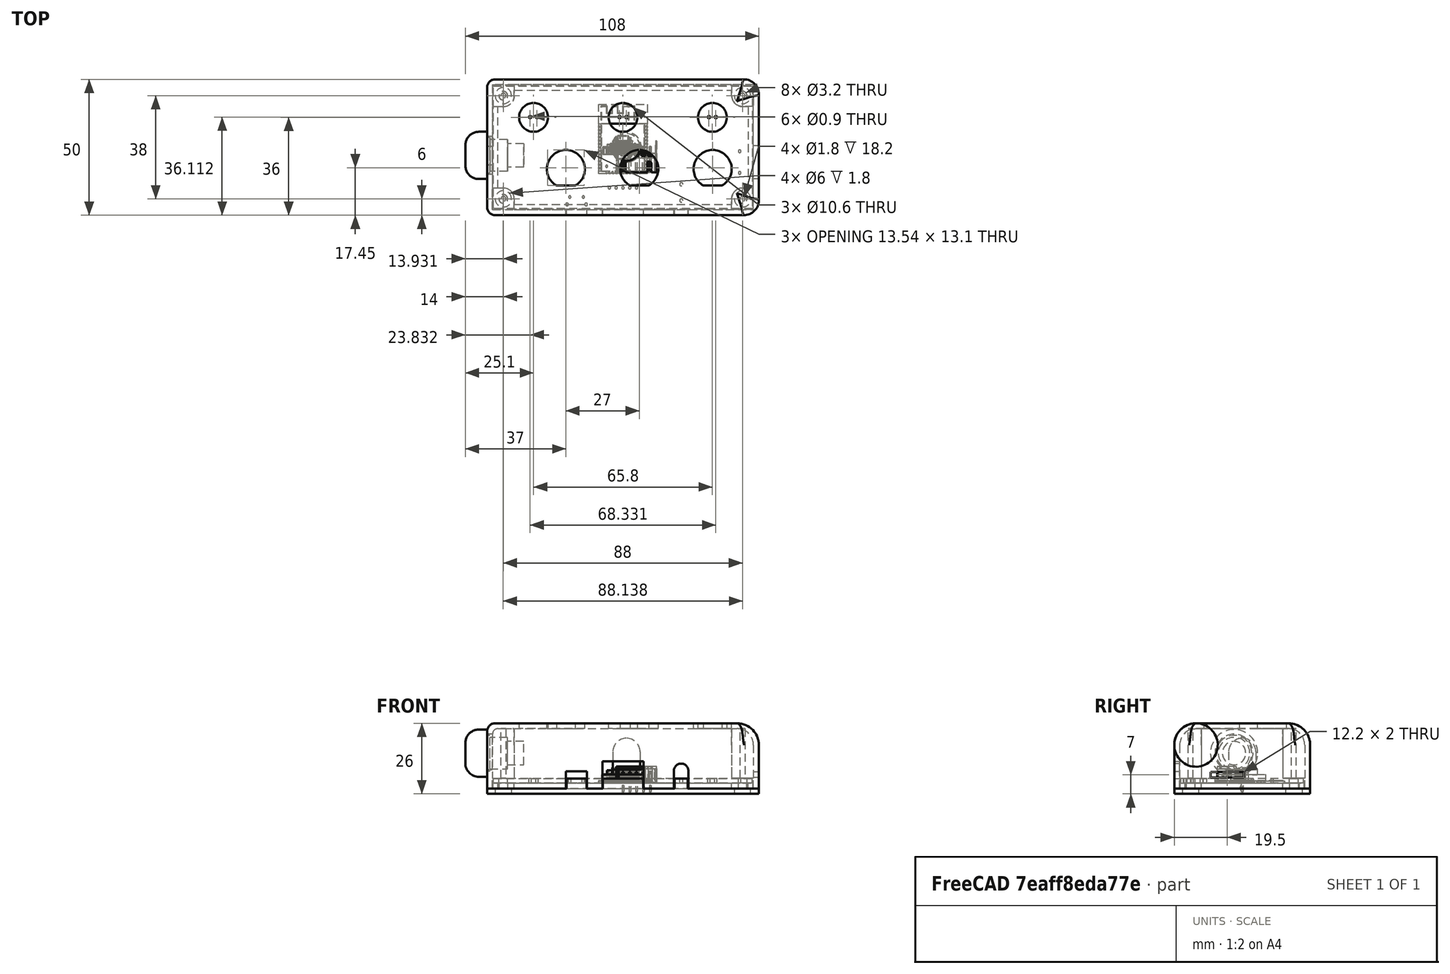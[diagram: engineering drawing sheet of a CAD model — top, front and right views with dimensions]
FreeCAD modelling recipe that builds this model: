
FCSTD DOCUMENT  (FreeCAD 0.21R33694 (Git))
Label: sigplane-head
License: All rights reserved
LicenseURL: http://en.wikipedia.org/wiki/All_rights_reserved
objects: Part::Feature×64, App::Part×58, Sketcher::SketchObject×16, PartDesign::Pad×9, PartDesign::Fillet×8, PartDesign::Pocket×7, PartDesign::Body×3, Part::FeaturePython×2, Mesh::Feature×1, App::DocumentObjectGroup×1
note: 132 computed .brp shape members not serialized (recipe doc carries the construction recipe); baked Part::Feature solids carry a one-line shape summary decoded from their .brp

FEATURE [Part::Feature] Part__Feature  label="SOLID"
  shape: bbox 2.5 x 3 x 1.2 mm, 76 faces (baked)
FEATURE [App::Part] SOT_23  label="SOT-23"
  Group = -> [Part__Feature]
  Origin = -> Origin
  Placement = pos=(20.265,16.3805,1.65) rot=(0,0,1;0rad)
FEATURE [Part::Feature] Part__Feature001  label="SOLID001"
  shape: bbox 2 x 1.2 x 0.45 mm, 26 faces (baked)
FEATURE [App::Part] R_0805_2012Metric
  Group = -> [Part__Feature001]
  Origin = -> Origin001
  Placement = pos=(-25.5505,-5.7785,1.65) rot=(0,0,1;0rad)
FEATURE [Part::Feature] Part__Feature002  label="SOLID002"
  shape: bbox 2 x 2 x 1.05 mm, 118 faces (baked)
FEATURE [App::Part] SOT_363_SC_70_6  label="SOT-363_SC-70-6"
  Group = -> [Part__Feature002]
  Origin = -> Origin002
  Placement = pos=(-20.762,-6.4135,1.65) rot=(0,0,1;0rad)
FEATURE [Part::Feature] Part__Feature003  label="SOLID003"
  shape: bbox 2 x 1.25 x 1.25 mm, 28 faces (baked)
FEATURE [App::Part] C_0805_2012Metric
  Group = -> [Part__Feature003]
  Origin = -> Origin003
  Placement = pos=(23.4885,10.2845,1.65) rot=(0,0,-1;1.5708rad)
FEATURE [Part::Feature] Part__Feature004  label="SOLID004"
  shape: bbox 15.15 x 4.2 x 4.7 mm, 267 faces (baked)
FEATURE [App::Part] Molex_PicoBlade_53398_0871_1x08_1MP_P1_25mm_Vertical  label="Molex_PicoBlade_53398-0871_1x08-1MP_P1.25mm_Vertical"
  Group = -> [Part__Feature004]
  Origin = -> Origin004
  Placement = pos=(-30.283,-18.7125,1.65) rot=(0,0,1;0rad)
FEATURE [Part::Feature] Part__Feature005  label="SOLID005"
  shape: bbox 3.2 x 1.6 x 0.55 mm, 26 faces (baked)
FEATURE [App::Part] R_1206_3216Metric
  Group = -> [Part__Feature005]
  Origin = -> Origin005
  Placement = pos=(4.699,19.4945,1.65) rot=(0,0,-1;1.5708rad)
FEATURE [Part::Feature] Part__Feature006  label="SOLID006"
  shape: bbox 2.5 x 1.25 x 1.1 mm, 67 faces (baked)
FEATURE [App::Part] D_SOD_323  label="D_SOD-323"
  Group = -> [Part__Feature006]
  Origin = -> Origin006
  Placement = pos=(4.953,-9.4275,1.65) rot=(0,0,-1;1.5708rad)
FEATURE [Part::Feature] Part__Feature007  label="SOLID007"
  shape: bbox 2 x 1.2 x 0.45 mm, 26 faces (baked)
FEATURE [App::Part] R_0805_2012Metric001
  Group = -> [Part__Feature007]
  Origin = -> Origin007
  Placement = pos=(-37.719,18.8595,1.65) rot=(0,0,-1;1.5708rad)
FEATURE [Part::Feature] Part__Feature008  label="SOLID008"
  shape: bbox 2 x 1.25 x 1.25 mm, 28 faces (baked)
FEATURE [App::Part] C_0805_2012Metric001
  Group = -> [Part__Feature008]
  Origin = -> Origin008
  Placement = pos=(-39.7455,2.6645,1.65) rot=(0,0,-1;1.5708rad)
FEATURE [Part::Feature] Part__Feature009  label="SOLID009"
  shape: bbox 2 x 1.25 x 1.25 mm, 28 faces (baked)
FEATURE [App::Part] C_0805_2012Metric002
  Group = -> [Part__Feature009]
  Origin = -> Origin009
  Placement = pos=(-32.004,-0.9525,1.65) rot=(0,0,-1;1.5708rad)
FEATURE [Part::Feature] Part__Feature010  label="SOLID010"
  shape: bbox 2 x 1.25 x 1.25 mm, 28 faces (baked)
FEATURE [App::Part] C_0805_2012Metric003
  Group = -> [Part__Feature010]
  Origin = -> Origin010
  Placement = pos=(23.4885,16.3805,1.65) rot=(0,0,-1;1.5708rad)
FEATURE [Part::Feature] Part__Feature011  label="SOLID011"
  shape: bbox 2.5 x 1.25 x 1.1 mm, 67 faces (baked)
FEATURE [App::Part] D_SOD_324  label="D_SOD-324"
  Group = -> [Part__Feature011]
  Origin = -> Origin011
  Placement = pos=(-25.5505,-14.2875,1.65) rot=(0,0,1;0rad)
FEATURE [Part::Feature] Part__Feature012  label="SOLID012"
  shape: bbox 2 x 1.25 x 1.25 mm, 28 faces (baked)
FEATURE [App::Part] C_0805_2012Metric004
  Group = -> [Part__Feature012]
  Origin = -> Origin012
  Placement = pos=(-20.701,-10.7315,1.65) rot=(0,0,-1;1.5708rad)
FEATURE [Part::Feature] Part__Feature013  label="SOLID013"
  shape: bbox 2 x 1.2 x 0.45 mm, 26 faces (baked)
FEATURE [App::Part] R_0805_2012Metric002
  Group = -> [Part__Feature013]
  Origin = -> Origin013
  Placement = pos=(-35.658,-11.517,1.65) rot=(0,0,-1;1.5708rad)
FEATURE [Part::Feature] Part__Feature014  label="SOLID014"
  shape: bbox 2 x 1.2 x 0.45 mm, 26 faces (baked)
FEATURE [App::Part] R_0805_2012Metric003
  Group = -> [Part__Feature014]
  Origin = -> Origin014
  Placement = pos=(9.9295,15.0445,1.65) rot=(0,0,1;0rad)
FEATURE [Part::Feature] Part__Feature015  label="SOLID015"
  shape: bbox 2 x 1.2 x 0.45 mm, 26 faces (baked)
FEATURE [App::Part] R_0805_2012Metric004
  Group = -> [Part__Feature015]
  Origin = -> Origin015
  Placement = pos=(-32.708,-11.517,1.65) rot=(0,0,-1;1.5708rad)
FEATURE [Part::Feature] Part__Feature016  label="SOLID016"
  shape: bbox 2 x 1.25 x 1.25 mm, 28 faces (baked)
FEATURE [App::Part] C_0805_2012Metric005
  Group = -> [Part__Feature016]
  Origin = -> Origin016
  Placement = pos=(19.939,-4.2545,1.65) rot=(0,0,1;3.14159rad)
FEATURE [Part::Feature] Part__Feature017  label="SOLID017"
  shape: bbox 6 x 8.7 x 1.65 mm, 396 faces (baked)
FEATURE [App::Part] SSOP_24_3_9x8_7mm_P0_635mm  label="SSOP-24_3.9x8.7mm_P0.635mm"
  Group = -> [Part__Feature017]
  Origin = -> Origin017
  Placement = pos=(16.0655,2.0285,1.65) rot=(0,0,-1;1.5708rad)
FEATURE [Part::Feature] Part__Feature018  label="SOLID018"
  shape: bbox 2 x 1.25 x 1.25 mm, 28 faces (baked)
FEATURE [App::Part] C_0805_2012Metric006
  Group = -> [Part__Feature018]
  Origin = -> Origin018
  Placement = pos=(-42.545,2.6645,1.65) rot=(0,0,-1;1.5708rad)
FEATURE [Part::Feature] Part__Feature019  label="SOLID019"
  shape: bbox 2 x 1.2 x 0.45 mm, 26 faces (baked)
FEATURE [App::Part] R_0805_2012Metric005
  Group = -> [Part__Feature019]
  Origin = -> Origin019
  Placement = pos=(30.353,18.836,1.65) rot=(0,0,-1;1.5708rad)
FEATURE [Part::Feature] Part__Feature020  label="SOLID020"
  shape: bbox 2 x 1.2 x 0.45 mm, 26 faces (baked)
FEATURE [App::Part] R_0805_2012Metric006
  Group = -> [Part__Feature020]
  Origin = -> Origin020
  Placement = pos=(9.923,11.0465,1.65) rot=(0,0,1;0rad)
FEATURE [Part::Feature] Part__Feature021  label="SOLID021"
  shape: bbox 3.2 x 1.6 x 0.55 mm, 26 faces (baked)
FEATURE [App::Part] R_1206_3216Metric001
  Group = -> [Part__Feature021]
  Origin = -> Origin021
  Placement = pos=(37.592,19.4945,1.65) rot=(0,0,-1;1.5708rad)
FEATURE [Part::Feature] Part__Feature022  label="SOLID022"
  shape: bbox 2 x 1.2 x 0.45 mm, 26 faces (baked)
FEATURE [App::Part] R_0805_2012Metric007
  Group = -> [Part__Feature022]
  Origin = -> Origin022
  Placement = pos=(6.477,1.2065,1.65) rot=(0,0,1;0rad)
FEATURE [Part::Feature] Part__Feature023  label="SOLID023"
  shape: bbox 2 x 1.2 x 0.45 mm, 26 faces (baked)
FEATURE [App::Part] R_0805_2012Metric008
  Group = -> [Part__Feature023]
  Origin = -> Origin023
  Placement = pos=(28.067,18.836,1.65) rot=(0,0,-1;1.5708rad)
FEATURE [Part::Feature] Part__Feature024  label="SOLID024"
  shape: bbox 2 x 1.2 x 0.45 mm, 26 faces (baked)
FEATURE [App::Part] R_0805_2012Metric009
  Group = -> [Part__Feature024]
  Origin = -> Origin024
  Placement = pos=(-2.54,18.883,1.65) rot=(0,0,-1;1.5708rad)
FEATURE [Part::Feature] Part__Feature025  label="SOLID025"
  shape: bbox 2.5 x 3 x 1.2 mm, 76 faces (baked)
FEATURE [App::Part] SOT_024  label="SOT-024"
  Group = -> [Part__Feature025]
  Origin = -> Origin025
  Placement = pos=(20.265,10.2895,1.65) rot=(0,0,1;0rad)
FEATURE [Part::Feature] Part__Feature026  label="SOLID026"
  shape: bbox 10.5 x 11 x 18.5 mm, 16 faces (baked)
FEATURE [App::Part] LED_D10_0mm  label="LED_D10.0mm"
  Group = -> [Part__Feature026]
  Origin = -> Origin026
  Placement = pos=(-1.275,11.1125,1.65) rot=(0,0,1;0rad)
FEATURE [Part::Feature] Part__Feature027  label="SOLID027"
  shape: bbox 2 x 1.2 x 0.45 mm, 26 faces (baked)
FEATURE [App::Part] R_0805_2012Metric010
  Group = -> [Part__Feature027]
  Origin = -> Origin027
  Placement = pos=(-10.414,-14.264,1.65) rot=(0,0,-1;1.5708rad)
FEATURE [Part::Feature] Part__Feature028  label="SOLID028"
  shape: bbox 2 x 1.2 x 0.45 mm, 26 faces (baked)
FEATURE [App::Part] R_0805_2012Metric011
  Group = -> [Part__Feature028]
  Origin = -> Origin028
  Placement = pos=(-35.433,18.8595,1.65) rot=(0,0,-1;1.5708rad)
FEATURE [Part::Feature] Part__Feature029  label="SOLID029"
  shape: bbox 2 x 1.2 x 0.45 mm, 26 faces (baked)
FEATURE [App::Part] R_0805_2012Metric012
  Group = -> [Part__Feature029]
  Origin = -> Origin029
  Placement = pos=(-4.826,18.883,1.65) rot=(0,0,-1;1.5708rad)
FEATURE [Part::Feature] Part__Feature030  label="SOLID030"
  shape: bbox 10.5 x 11 x 18.5 mm, 16 faces (baked)
FEATURE [App::Part] LED_D10_0mm001  label="LED_D10.0mm001"
  Group = -> [Part__Feature030]
  Origin = -> Origin030
  Placement = pos=(-34.168,11.1125,1.65) rot=(0,0,1;0rad)
FEATURE [Part::Feature] Part__Feature031  label="SOLID031"
  shape: bbox 2 x 1.2 x 0.45 mm, 26 faces (baked)
FEATURE [App::Part] R_0805_2012Metric013
  Group = -> [Part__Feature031]
  Origin = -> Origin031
  Placement = pos=(-13.208,-14.264,1.65) rot=(0,0,-1;1.5708rad)
FEATURE [Part::Feature] Part__Feature032  label="SOLID032"
  shape: bbox 2 x 1.2 x 0.45 mm, 26 faces (baked)
FEATURE [App::Part] R_0805_2012Metric014
  Group = -> [Part__Feature032]
  Origin = -> Origin032
  Placement = pos=(-29.758,-11.517,1.65) rot=(0,0,-1;1.5708rad)
FEATURE [Part::Feature] Part__Feature033  label="SOLID033"
  shape: bbox 2.5 x 3 x 1.2 mm, 76 faces (baked)
FEATURE [App::Part] SOT_025  label="SOT-025"
  Group = -> [Part__Feature033]
  Origin = -> Origin033
  Placement = pos=(13.818,16.4415,1.65) rot=(0,0,1;0rad)
FEATURE [Part::Feature] Part__Feature034  label="SOLID034"
  shape: bbox 5 x 5 x 0.92 mm, 182 faces (baked)
FEATURE [App::Part] QFN_28_1EP_5x5mm_P0_5mm_EP3_35x3_35mm  label="QFN-28-1EP_5x5mm_P0.5mm_EP3.35x3.35mm"
  Group = -> [Part__Feature034]
  Origin = -> Origin034
  Placement = pos=(-13.499,-8.8505,1.65) rot=(0,0,1;0rad)
FEATURE [Part::Feature] Part__Feature035  label="SOLID035"
  shape: bbox 2 x 1.2 x 0.45 mm, 26 faces (baked)
FEATURE [App::Part] R_0805_2012Metric015
  Group = -> [Part__Feature035]
  Origin = -> Origin035
  Placement = pos=(-38.608,-11.517,1.65) rot=(0,0,-1;1.5708rad)
FEATURE [Part::Feature] Part__Feature036  label="SOLID036"
  shape: bbox 3.2 x 1.6 x 0.55 mm, 26 faces (baked)
FEATURE [App::Part] R_1206_3216Metric002
  Group = -> [Part__Feature036]
  Origin = -> Origin036
  Placement = pos=(-28.194,19.4945,1.65) rot=(0,0,-1;1.5708rad)
FEATURE [Part::Feature] Part__Feature037  label="SOLID037"
  shape: bbox 2 x 1.2 x 0.45 mm, 26 faces (baked)
FEATURE [App::Part] R_0805_2012Metric016
  Group = -> [Part__Feature037]
  Origin = -> Origin037
  Placement = pos=(17.0115,10.261,1.65) rot=(0,0,-1;1.5708rad)
FEATURE [Part::Feature] Part__Feature038  label="SOLID038"
  shape: bbox 2 x 1.2 x 0.45 mm, 26 faces (baked)
FEATURE [App::Part] R_0805_2012Metric017
  Group = -> [Part__Feature038]
  Origin = -> Origin038
  Placement = pos=(-7.493,-7.9375,1.65) rot=(0,0,1;0rad)
FEATURE [Part::Feature] Part__Feature039  label="SOLID039"
  shape: bbox 14.9 x 11.5 x 9.5 mm, 193 faces (baked)
FEATURE [App::Part] JST_XH_S5B_XH_A_1x05_P2_50mm_Horizontal  label="JST_XH_S5B-XH-A_1x05_P2.50mm_Horizontal"
  Group = -> [Part__Feature039]
  Origin = -> Origin039
  Placement = pos=(-5,-14.9015,1.65) rot=(0,0,1;0rad)
FEATURE [Part::Feature] Part__Feature040  label="SOLID040"
  shape: bbox 2 x 1.2 x 0.45 mm, 26 faces (baked)
FEATURE [App::Part] R_0805_2012Metric018
  Group = -> [Part__Feature040]
  Origin = -> Origin040
  Placement = pos=(-32.004,2.7305,1.65) rot=(0,0,-1;1.5708rad)
FEATURE [Part::Feature] Part__Feature041  label="SOLID041"
  shape: bbox 2.5 x 3 x 1.2 mm, 76 faces (baked)
FEATURE [App::Part] SOT_026  label="SOT-026"
  Group = -> [Part__Feature041]
  Origin = -> Origin041
  Placement = pos=(-31.623,19.827,1.65) rot=(0,0,1;1.5708rad)
FEATURE [Part::Feature] Part__Feature042  label="SOLID042"
  shape: bbox 2.5 x 1.25 x 1.1 mm, 67 faces (baked)
FEATURE [App::Part] D_SOD_325  label="D_SOD-325"
  Group = -> [Part__Feature042]
  Origin = -> Origin042
  Placement = pos=(-25.5505,-9.8425,1.65) rot=(0,0,1;0rad)
FEATURE [Part::Feature] Part__Feature043  label="SOLID043"
  shape: bbox 2 x 1.2 x 0.45 mm, 26 faces (baked)
FEATURE [App::Part] R_0805_2012Metric019
  Group = -> [Part__Feature043]
  Origin = -> Origin043
  Placement = pos=(9.9295,17.2035,1.65) rot=(0,0,1;0rad)
FEATURE [Part::Feature] Part__Feature044  label="SOLID044"
  shape: bbox 2 x 1.25 x 1.25 mm, 28 faces (baked)
FEATURE [App::Part] C_0805_2012Metric007
  Group = -> [Part__Feature044]
  Origin = -> Origin044
  Placement = pos=(29.591,-6.6675,1.65) rot=(0,0,-1;1.5708rad)
FEATURE [Part::Feature] Part__Feature045  label="SOLID045"
  shape: bbox 2 x 1.2 x 0.45 mm, 26 faces (baked)
FEATURE [App::Part] R_0805_2012Metric020
  Group = -> [Part__Feature045]
  Origin = -> Origin045
  Placement = pos=(17.0415,16.4415,1.65) rot=(0,0,-1;1.5708rad)
FEATURE [Part::Feature] Part__Feature046  label="SOLID046"
  shape: bbox 2 x 1.25 x 1.25 mm, 28 faces (baked)
FEATURE [App::Part] C_0805_2012Metric008
  Group = -> [Part__Feature046]
  Origin = -> Origin046
  Placement = pos=(-20.701,-14.5415,1.65) rot=(0,0,-1;1.5708rad)
FEATURE [Part::Feature] Part__Feature047  label="SOLID047"
  shape: bbox 2.5 x 3 x 1.2 mm, 76 faces (baked)
FEATURE [App::Part] SOT_027  label="SOT-027"
  Group = -> [Part__Feature047]
  Origin = -> Origin047
  Placement = pos=(34.163,19.827,1.65) rot=(0,0,1;1.5708rad)
FEATURE [Part::Feature] Part__Feature048  label="SOLID048"
  shape: bbox 2 x 1.2 x 0.45 mm, 26 faces (baked)
FEATURE [App::Part] R_0805_2012Metric021
  Group = -> [Part__Feature048]
  Origin = -> Origin048
  Placement = pos=(6.477,3.2385,1.65) rot=(0,0,1;0rad)
FEATURE [Part::Feature] Part__Feature049  label="SOLID049"
  shape: bbox 2 x 1.2 x 0.45 mm, 26 faces (baked)
FEATURE [App::Part] R_0805_2012Metric022
  Group = -> [Part__Feature049]
  Origin = -> Origin049
  Placement = pos=(-7.493,-5.7785,1.65) rot=(0,0,1;0rad)
FEATURE [Part::Feature] Part__Feature050  label="SOLID050"
  shape: bbox 7.5 x 4.6 x 2 mm, 40 faces (baked)
FEATURE [App::Part] CP_EIA_7343_20_Kemet_V  label="CP_EIA-7343-20_Kemet-V"
  Group = -> [Part__Feature050]
  Origin = -> Origin050
  Placement = pos=(-35.687,0.5715,1.65) rot=(0,0,-1;1.5708rad)
FEATURE [Part::Feature] Part__Feature051  label="SOLID051"
  shape: bbox 18 x 25.5 x 3.1 mm, 751 faces (baked)
FEATURE [App::Part] ESP32_WROOM_32  label="ESP32-WROOM-32"
  Group = -> [Part__Feature051]
  Origin = -> Origin051
  Placement = pos=(-16.337,6.5455,1.65) rot=(0,0,1;0rad)
FEATURE [Part::Feature] Part__Feature052  label="SOLID052"
  shape: bbox 10.5 x 11 x 18.5 mm, 16 faces (baked)
FEATURE [App::Part] LED_D10_0mm002  label="LED_D10.0mm002"
  Group = -> [Part__Feature052]
  Origin = -> Origin052
  Placement = pos=(31.623,11.1125,1.65) rot=(0,0,1;0rad)
FEATURE [Part::Feature] Part__Feature053  label="SOLID053"
  shape: bbox 2.8 x 2.9 x 1.55 mm, 109 faces (baked)
FEATURE [App::Part] SOT_23_5  label="SOT-23-5"
  Group = -> [Part__Feature053]
  Origin = -> Origin053
  Placement = pos=(-40.767,6.9215,1.65) rot=(0,0,-1;1.5708rad)
FEATURE [Part::Feature] Part__Feature054  label="SOLID054"
  shape: bbox 2.5 x 3 x 1.2 mm, 76 faces (baked)
FEATURE [App::Part] SOT_028  label="SOT-028"
  Group = -> [Part__Feature054]
  Origin = -> Origin054
  Placement = pos=(1.27,19.827,1.65) rot=(0,0,1;1.5708rad)
FEATURE [Part::Feature] Part__Feature055  label="SOLID055"
  shape: bbox 2.5 x 3 x 1.2 mm, 76 faces (baked)
FEATURE [App::Part] SOT_029  label="SOT-029"
  Group = -> [Part__Feature055]
  Origin = -> Origin055
  Placement = pos=(13.758,10.2185,1.65) rot=(0,0,1;0rad)
FEATURE [Part::Feature] Part__Feature056  label="sigplane-head PCB"
  shape: bbox 95.25 x 45.09 x 1.6 mm, 67 faces (baked)
FEATURE [App::Part] sigplane_head_1  label="sigplane-head 1"
  Group = -> [SOT_23,R_0805_2012Metric,SOT_363_SC_70_6,C_0805_2012Metric,Molex_PicoBlade_53398_0871_1x08_1MP_P1_25mm_Vertical,R_1206_3216Metric,D_SOD_323,R_0805_2012Metric001,C_0805_2012Metric001,C_0805_2012Metric002,C_0805_2012Metric003,D_SOD_324,C_0805_2012Metric004,R_0805_2012Metric002,R_0805_2012Metric003,R_0805_2012Metric004,C_0805_2012Metric005,SSOP_24_3_9x8_7mm_P0_635mm,C_0805_2012Metric006,+38 more]
  Origin = -> Origin056
FEATURE [Mesh::Feature] microsd
  Placement = pos=(31.7,-12.5,1.1) rot=(0.57735,0.57735,0.57735;2.0944rad)
FEATURE [Part::Feature] Part__Feature057  label="Micro USB-B Female 5Pin SMD"
  shape: bbox 0.3 x 1.55 x 4.2 mm, 15 faces (baked)
FEATURE [Part::Feature] Part__Feature058  label="Micro USB-B Female 5Pin SMD001"
  shape: bbox 0.3 x 1.55 x 4.2 mm, 15 faces (baked)
FEATURE [Part::Feature] Part__Feature059  label="Micro USB-B Female 5Pin SMD002"
  shape: bbox 0.3 x 1.55 x 4.2 mm, 15 faces (baked)
FEATURE [Part::Feature] Part__Feature060  label="Micro USB-B Female 5Pin SMD003"
  shape: bbox 0.3 x 1.55 x 4.2 mm, 15 faces (baked)
FEATURE [Part::Feature] Part__Feature061  label="Micro USB-B Female 5Pin SMD004"
  shape: bbox 0.3 x 1.55 x 4.2 mm, 15 faces (baked)
FEATURE [Part::Feature] Part__Feature062  label="Micro USB-B Female 5Pin SMD005"
  shape: bbox 6.9 x 2.4 x 4.15 mm, 176 faces (baked)
FEATURE [Part::Feature] Part__Feature063  label="Micro USB-B Female 5Pin SMD006"
  shape: bbox 8.172 x 3.786 x 5.619 mm, 257 faces (baked)
FEATURE [App::Part] Micro_USB_B_Female_5Pin_SMD  label="Micro USB-B Female 5Pin SMD007"
  Group = -> [Part__Feature057,Part__Feature058,Part__Feature059,Part__Feature060,Part__Feature061,Part__Feature062,Part__Feature063]
  Origin = -> Origin057
  Placement = pos=(-17.1,-18.1,2.85) rot=(1,0,0;1.5708rad)
FEATURE [Sketcher::SketchObject] Sketch  label="основные габариты"
  AttachmentOffset = pos=(0,0,-2) rot=(0,0,1;0rad)
  FullyConstrained = true
  MapMode = 5
  Placement = pos=(0,0,-2) rot=(0,0,1;0rad)
  Support = -> [XY_Plane058]
  sketch-geometry (4):
    g0: LineSegment StartX=-50 StartY=25 StartZ=0 EndX=50 EndY=25 EndZ=0
    g1: LineSegment StartX=50 StartY=25 StartZ=0 EndX=50 EndY=-25 EndZ=0
    g2: LineSegment StartX=50 StartY=-25 StartZ=0 EndX=-50 EndY=-25 EndZ=0
    g3: LineSegment StartX=-50 StartY=-25 StartZ=0 EndX=-50 EndY=25 EndZ=0
  constraints (11):
    c: Coincident(g0,g1)
    c: Coincident(g1,g2)
    c: Coincident(g2,g3)
    c: Coincident(g3,g0)
    c: Horizontal(g0)
    c: Horizontal(g2)
    c: Vertical(g1)
    c: Vertical(g3)
    c: Symmetric(g0,g1,g-1)
    c: Distance(g0) = 100
    c: Distance(g3) = 50
FEATURE [PartDesign::Pad] Pad
  Direction = (0,0,1)
  Length = 24
  Length2 = 10
  Profile = -> Sketch
  ReferenceAxis = -> Sketch [N_Axis]
  Type = 0
FEATURE [Sketcher::SketchObject] Sketch001  label="внутр"
  FullyConstrained = true
  MapMode = 5
  Placement = pos=(0,0,-2) rot=(1,0,0;3.14159rad)
  Support = -> [Pad]
  sketch-geometry (4):
    g0: LineSegment StartX=-48 StartY=23 StartZ=0 EndX=48 EndY=23 EndZ=0
    g1: LineSegment StartX=48 StartY=23 StartZ=0 EndX=48 EndY=-23 EndZ=0
    g2: LineSegment StartX=48 StartY=-23 StartZ=0 EndX=-48 EndY=-23 EndZ=0
    g3: LineSegment StartX=-48 StartY=-23 StartZ=0 EndX=-48 EndY=23 EndZ=0
  constraints (11):
    c: Coincident(g0,g1)
    c: Coincident(g1,g2)
    c: Coincident(g2,g3)
    c: Coincident(g3,g0)
    c: Horizontal(g0)
    c: Horizontal(g2)
    c: Vertical(g1)
    c: Vertical(g3)
    c: Distance(g3) = 46
    c: Distance(g0) = 96
    c: Symmetric(g0,g1,g-1)
FEATURE [PartDesign::Pocket] Pocket
  BaseFeature = -> Pad
  Direction = (0,0,1)
  Length = 22
  Length2 = 5
  Profile = -> Sketch001
  ReferenceAxis = -> Sketch001 [N_Axis]
  Type = 0
FEATURE [Sketcher::SketchObject] Sketch002
  ExternalGeometry = -> [Pocket]
  FullyConstrained = true
  MapMode = 5
  Placement = pos=(0,0,20) rot=(1,0,0;3.14159rad)
  Support = -> [Pocket]
  sketch-geometry (24):
    g0: LineSegment StartX=-48 StartY=23 StartZ=0 EndX=-40 EndY=23 EndZ=0
    g1: LineSegment StartX=-48 StartY=23 StartZ=0 EndX=-48 EndY=15 EndZ=0
    g2: Circle CenterX=-44 CenterY=19 CenterZ=0 NormalX=0 NormalY=0 NormalZ=1 AngleXU=0 Radius=0.9
    g3: ArcOfCircle CenterX=-44 CenterY=19 CenterZ=0 NormalX=0 NormalY=0 NormalZ=1 AngleXU=0 Radius=4 StartAngle=4.71239 EndAngle=6.28319
    g4: LineSegment StartX=-48 StartY=15 StartZ=0 EndX=-44 EndY=15 EndZ=0
    g5: LineSegment StartX=-40 StartY=23 StartZ=0 EndX=-40 EndY=19 EndZ=0
    g6: ArcOfCircle CenterX=44 CenterY=19 CenterZ=0 NormalX=0 NormalY=0 NormalZ=1 AngleXU=0 Radius=4 StartAngle=3.14159 EndAngle=4.71239
    g7: LineSegment StartX=48 StartY=23 StartZ=0 EndX=40 EndY=23 EndZ=0
    g8: LineSegment StartX=40 StartY=23 StartZ=0 EndX=40 EndY=19 EndZ=0
    g9: LineSegment StartX=48 StartY=23 StartZ=0 EndX=48 EndY=15 EndZ=0
    g10: LineSegment StartX=48 StartY=15 StartZ=0 EndX=44 EndY=15 EndZ=0
    g11: Circle CenterX=44 CenterY=19 CenterZ=0 NormalX=0 NormalY=0 NormalZ=1 AngleXU=0 Radius=0.9
    g12: ArcOfCircle CenterX=-44 CenterY=-19 CenterZ=0 NormalX=0 NormalY=0 NormalZ=1 AngleXU=0 Radius=4 StartAngle=0 EndAngle=1.5708
    g13: LineSegment StartX=-48 StartY=-23 StartZ=0 EndX=-40 EndY=-23 EndZ=0
    g14: LineSegment StartX=-40 StartY=-23 StartZ=0 EndX=-40 EndY=-19 EndZ=0
    g15: LineSegment StartX=-48 StartY=-23 StartZ=0 EndX=-48 EndY=-15 EndZ=0
    g16: LineSegment StartX=-48 StartY=-15 StartZ=0 EndX=-44 EndY=-15 EndZ=0
    g17: Circle CenterX=-44 CenterY=-19 CenterZ=0 NormalX=0 NormalY=0 NormalZ=1 AngleXU=0 Radius=0.9
    g18: ArcOfCircle CenterX=44 CenterY=-19 CenterZ=0 NormalX=0 NormalY=0 NormalZ=1 AngleXU=0 Radius=4 StartAngle=1.5708 EndAngle=3.14159
    g19: LineSegment StartX=48 StartY=-23 StartZ=0 EndX=48 EndY=-15 EndZ=0
    g20: LineSegment StartX=48 StartY=-15 StartZ=0 EndX=44 EndY=-15 EndZ=0
    g21: LineSegment StartX=48 StartY=-23 StartZ=0 EndX=40 EndY=-23 EndZ=0
    g22: LineSegment StartX=40 StartY=-23 StartZ=0 EndX=40 EndY=-19 EndZ=0
    g23: Circle CenterX=44 CenterY=-19 CenterZ=0 NormalX=0 NormalY=0 NormalZ=1 AngleXU=0 Radius=0.9
  constraints (70):
    c: Coincident(g0,g-3)
    c: Horizontal(g0)
    c: Coincident(g1,g0)
    c: Vertical(g1)
    c: Radius(g2) = 0.9
    c: DistanceX(g0,g2) = 4
    c: DistanceY(g2,g0) = 4
    c: Coincident(g3,g2)
    c: Coincident(g3,g0)
    c: Coincident(g3,g1)
    c: Radius(g3) = 4
    c: Coincident(g4,g1)
    c: Horizontal(g4)
    c: Coincident(g5,g0)
    c: Vertical(g5)
    c: Distance(g5) = 4
    c: Distance(g4) = 4
    c: Coincident(g3,g5)
    c: Coincident(g3,g4)
    c: Radius(g6) = 4
    c: DistanceX(g6,g-6) = 4
    c: DistanceY(g6,g-6) = 4
    c: Coincident(g7,g-6)
    c: Horizontal(g7)
    c: Coincident(g8,g7)
    c: Vertical(g8)
    c: Coincident(g9,g7)
    c: Vertical(g9)
    c: Coincident(g10,g9)
    c: Horizontal(g10)
    c: Distance(g8) = 4
    c: Distance(g10) = 4
    c: Coincident(g6,g8)
    c: Coincident(g6,g10)
    c: Coincident(g11,g6)
    c: Radius(g11) = 0.9
    c: Radius(g12) = 4
    c: DistanceY(g-4,g12) = 4
    c: DistanceX(g-4,g12) = 4
    c: Coincident(g13,g-4)
    c: Horizontal(g13)
    c: Coincident(g14,g13)
    c: Vertical(g14)
    c: Coincident(g15,g13)
    c: Vertical(g15)
    c: Coincident(g16,g15)
    c: Horizontal(g16)
    c: Distance(g16) = 4
    c: Distance(g14) = 4
    c: Coincident(g12,g16)
    c: Coincident(g12,g14)
    c: Coincident(g17,g12)
    c: Radius(g17) = 0.9
    c: Radius(g18) = 4
    c: DistanceY(g-5,g18) = 4
    c: DistanceX(g18,g-5) = 4
    c: Coincident(g19,g-5)
    c: Vertical(g19)
    c: Coincident(g20,g19)
    c: Horizontal(g20)
    c: Coincident(g21,g19)
    c: Horizontal(g21)
    c: Vertical(g22)
    c: Distance(g22) = 4
    c: Distance(g20) = 4
    c: Coincident(g20,g18)
    c: Coincident(g18,g22)
    c: Coincident(g23,g18)
    c: Radius(g23) = 0.9
    c: Coincident(g22,g21)
FEATURE [PartDesign::Pad] Pad001  label="стойки винтов"
  BaseFeature = -> Pocket
  Direction = (0,0,-1)
  Length = 18.2
  Length2 = 10
  Profile = -> Sketch002
  ReferenceAxis = -> Sketch002 [N_Axis]
  Type = 0
FEATURE [Sketcher::SketchObject] Sketch003  label="резьба"
  FullyConstrained = true
  MapMode = 5
  Support = -> [XY_Plane059]
  sketch-geometry (1):
    g0: Circle CenterX=0 CenterY=0 CenterZ=0 NormalX=0 NormalY=0 NormalZ=1 AngleXU=0 Radius=5.8
  constraints (2):
    c: Coincident(g0,g-1)
    c: Diameter(g0) = 11.6
FEATURE [PartDesign::Pad] Pad002  label="pad-резьба"
  Direction = (0,0,1)
  Length = 7.5
  Length2 = 10
  Profile = -> Sketch003
  ReferenceAxis = -> Sketch003 [N_Axis]
  Type = 0
FEATURE [Sketcher::SketchObject] Sketch004  label="верхняя выпуклость"
  FullyConstrained = true
  MapMode = 5
  Support = -> [XY_Plane059]
  sketch-geometry (1):
    g0: Circle CenterX=0 CenterY=0 CenterZ=0 NormalX=0 NormalY=0 NormalZ=1 AngleXU=0 Radius=8.7
  constraints (2):
    c: Coincident(g0,g-1)
    c: Diameter(g0) = 17.4
FEATURE [PartDesign::Pad] Pad003  label="pad-верх"
  BaseFeature = -> Pad002
  Direction = (0,0,1)
  Length = 8
  Length2 = 10
  Profile = -> Sketch004
  ReferenceAxis = -> Sketch004 [N_Axis]
  Reversed = true
  Type = 0
  UseCustomVector = true
FEATURE [Sketcher::SketchObject] Sketch005  label="венец у резьбы"
  FullyConstrained = true
  MapMode = 5
  Support = -> [XY_Plane059]
  sketch-geometry (1):
    g0: Circle CenterX=0 CenterY=0 CenterZ=0 NormalX=0 NormalY=0 NormalZ=1 AngleXU=0 Radius=6.55
  constraints (2):
    c: Coincident(g0,g-1)
    c: Diameter(g0) = 13.1
FEATURE [PartDesign::Pad] Pad004  label="pad-венец"
  BaseFeature = -> Pad003
  Direction = (0,0,1)
  Length = 1
  Length2 = 10
  Profile = -> Sketch005
  ReferenceAxis = -> Sketch005 [N_Axis]
  Type = 0
FEATURE [Sketcher::SketchObject] Sketch007  label="контакты"
  FullyConstrained = true
  MapMode = 5
  Placement = pos=(0,0,7.5) rot=(0,0,1;0rad)
  Support = -> [Pad002]
  sketch-geometry (1):
    g0: Circle CenterX=0 CenterY=0 CenterZ=0 NormalX=0 NormalY=0 NormalZ=1 AngleXU=0 Radius=4.3
  constraints (2):
    c: Coincident(g0,g-1)
    c: Diameter(g0) = 8.6
FEATURE [PartDesign::Pad] Pad005  label="pad-контакты"
  BaseFeature = -> Pad004
  Direction = (0,0,1)
  Length = 6
  Length2 = 10
  Profile = -> Sketch007
  ReferenceAxis = -> Sketch007 [N_Axis]
  Type = 0
FEATURE [PartDesign::Fillet] Fillet002  label="Fill-верх"
  Base = -> Pad005 [Face3]
  BaseFeature = -> Pad005
  Radius = 5
  SupportTransform = false
  UseAllEdges = false
FEATURE [PartDesign::Body] Body001  label="кнопка"
  Group = -> [Sketch003,Sketch004,Pad002,Pad003,Sketch005,Pad004,Sketch007,Pad005,Fillet002]
  Origin = -> Origin059
  Placement = pos=(0,0,22) rot=(0,1,0;3.14159rad)
  Tip = -> Fillet002
FEATURE [Part::FeaturePython] Array  # Draft array (typed FeaturePython)
  AlwaysSyncPlacement = false
  Angle = 360
  ArrayType = 0
  Axis = (0,0,1)
  Base = -> Body001
  Center = (0,0,0)
  Count = 3
  ExpandArray = false
  Fuse = false
  IntervalAxis = (0,0,0)
  IntervalX = (27,0,0)
  IntervalY = (0,100,0)
  IntervalZ = (0,0,100)
  NumberCircles = 3
  NumberPolar = 5
  NumberX = 3
  NumberY = 1
  NumberZ = 1
  Placement = pos=(-21,-8,0) rot=(0,0,1;0rad)
  PlacementList = 3 placements: arithmetic series from (0,0,22) step (27,0,0) to (54,0,22)
  RadialDistance = 50
  ScaleList = (3) [(1,1,1),(1,1,1),(1,1,1)]
  Symmetry = 1
  TangentialDistance = 25
FEATURE [Part::FeaturePython] Clone  label="кнопка001"  # Draft clone (typed FeaturePython)
  AttacherType = Attacher::AttachEngine3D
  Fuse = false
  Objects = -> [Body001]
  Placement = pos=(-50,-3,11) rot=(0,1,0;1.5708rad)
  Scale = (1,1,1)
FEATURE [App::DocumentObjectGroup] Group  label="содержимое"
  Group = -> [sigplane_head_1,Micro_USB_B_Female_5Pin_SMD,microsd,Body001,Array,Clone]
FEATURE [Sketcher::SketchObject] Sketch008
  ExternalGeometry = -> [Pad001]
  FullyConstrained = true
  MapMode = 5
  Placement = pos=(0,0,22) rot=(0,0,1;0rad)
  Support = -> [Pad001]
  sketch-geometry (9):
    g0: Circle CenterX=-32.9 CenterY=11 CenterZ=0 NormalX=0 NormalY=0 NormalZ=1 AngleXU=0 Radius=5.3
    g1: Circle CenterX=4e-16 CenterY=11 CenterZ=0 NormalX=0 NormalY=0 NormalZ=1 AngleXU=0 Radius=5.3
    g2: Circle CenterX=32.9 CenterY=11 CenterZ=0 NormalX=0 NormalY=0 NormalZ=1 AngleXU=0 Radius=5.3
    g3: ArcOfCircle CenterX=-21 CenterY=-8 CenterZ=0 NormalX=0 NormalY=0 NormalZ=1 AngleXU=0 Radius=7 StartAngle=5.22508 EndAngle=10.4829
    g4: ArcOfCircle CenterX=6 CenterY=-8 CenterZ=0 NormalX=0 NormalY=0 NormalZ=1 AngleXU=0 Radius=7 StartAngle=5.22508 EndAngle=10.4829
    g5: ArcOfCircle CenterX=33 CenterY=-8 CenterZ=0 NormalX=0 NormalY=0 NormalZ=1 AngleXU=0 Radius=7 StartAngle=5.22508 EndAngle=10.4829
    g6: LineSegment StartX=-24.4337 StartY=-14.1 StartZ=0 EndX=-17.5663 EndY=-14.1 EndZ=0
    g7: LineSegment StartX=2.56634 StartY=-14.1 StartZ=0 EndX=9.43366 EndY=-14.1 EndZ=0
    g8: LineSegment StartX=29.5663 StartY=-14.1 StartZ=0 EndX=36.4337 EndY=-14.1 EndZ=0
  constraints (30):
    c: PointOnObject(g1,g-2)
    c: Radius(g0) = 5.3
    c: Radius(g1) = 5.3
    c: Radius(g2) = 5.3
    c: DistanceY(g0,g-3) = 14
    c: Horizontal(g0,g1)
    c: Horizontal(g1,g2)
    c: Distance(g1,g0) = 32.9
    c: Distance(g1,g2) = 32.9
    c: Horizontal(g3,g4)
    c: Horizontal(g4,g5)
    c: DistanceY(g3,g-1) = 8
    c: DistanceX(g3,g-1) = 21
    c: Distance(g3,g4) = 27
    c: Distance(g4,g5) = 27
    c: Radius(g3) = 7
    c: Radius(g4) = 7
    c: Radius(g5) = 7
    c: Coincident(g6,g3)
    c: Horizontal(g6)
    c: Coincident(g7,g4)
    c: Horizontal(g7)
    c: Coincident(g8,g5)
    c: Horizontal(g8)
    c: Coincident(g6,g3)
    c: Coincident(g7,g4)
    c: Coincident(g8,g5)
    c: DistanceY(g3,g3) = 6.1
    c: DistanceY(g4,g4) = 6.1
    c: DistanceY(g5,g5) = 6.1
FEATURE [PartDesign::Pocket] Pocket001  label="отверстия верх"
  BaseFeature = -> Pad001
  Direction = (0,0,-1)
  Length = 2
  Length2 = 5
  Profile = -> Sketch008
  ReferenceAxis = -> Sketch008 [N_Axis]
  Type = 0
FEATURE [Sketcher::SketchObject] Sketch009
  FullyConstrained = true
  MapMode = 5
  Placement = pos=(-50,0,0) rot=(0.57735,-0.57735,-0.57735;2.0944rad)
  Support = -> [Pocket001]
  sketch-geometry (2):
    g0: ArcOfCircle CenterX=3 CenterY=11 CenterZ=0 NormalX=0 NormalY=0 NormalZ=1 AngleXU=0 Radius=7 StartAngle=5.22508 EndAngle=10.4829
    g1: LineSegment StartX=-0.433657 StartY=4.9 StartZ=0 EndX=6.43366 EndY=4.9 EndZ=0
  constraints (7):
    c: Radius(g0) = 7
    c: DistanceY(g-1,g0) = 11
    c: DistanceX(g-1,g0) = 3
    c: Coincident(g1,g0)
    c: Horizontal(g1)
    c: Coincident(g1,g0)
    c: DistanceY(g0,g0) = 6.1
FEATURE [PartDesign::Pocket] Pocket002  label="отверстия бок кнопка"
  BaseFeature = -> Pocket001
  Direction = (1,0,0)
  Length = 2
  Length2 = 5
  Profile = -> Sketch009
  ReferenceAxis = -> Sketch009 [N_Axis]
  Type = 0
FEATURE [Sketcher::SketchObject] Sketch010
  ExternalGeometry = -> [Pocket002]
  FullyConstrained = true
  MapMode = 5
  Placement = pos=(50,0,0) rot=(0.57735,0.57735,0.57735;2.0944rad)
  Support = -> [Pocket002]
  sketch-geometry (4):
    g0: LineSegment StartX=-11.6 StartY=2 StartZ=0 EndX=0.6 EndY=2 EndZ=0
    g1: LineSegment StartX=0.6 StartY=2 StartZ=0 EndX=0.6 EndY=4 EndZ=0
    g2: LineSegment StartX=0.6 StartY=4 StartZ=0 EndX=-11.6 EndY=4 EndZ=0
    g3: LineSegment StartX=-11.6 StartY=4 StartZ=0 EndX=-11.6 EndY=2 EndZ=0
  constraints (12):
    c: Coincident(g0,g1)
    c: Coincident(g1,g2)
    c: Coincident(g2,g3)
    c: Coincident(g3,g0)
    c: Horizontal(g0)
    c: Horizontal(g2)
    c: Vertical(g1)
    c: Vertical(g3)
    c: Distance(g2) = 12.2
    c: DistanceX(g-1,g0) = 0.6
    c: DistanceY(g-1,g1) = 4
    c: DistanceY(g-1,g0) = 2
FEATURE [PartDesign::Pocket] Pocket003  label="отверстия sdcard"
  BaseFeature = -> Pocket002
  Direction = (-1,0,0)
  Length = 2
  Length2 = 5
  Profile = -> Sketch010
  ReferenceAxis = -> Sketch010 [N_Axis]
  Type = 0
FEATURE [Sketcher::SketchObject] Sketch011
  FullyConstrained = true
  MapMode = 5
  Placement = pos=(0,-25,0) rot=(1,0,0;1.5708rad)
  Support = -> [Pocket003]
  sketch-geometry (14):
    g0: LineSegment StartX=-21 StartY=-2 StartZ=0 EndX=-13.2 EndY=-2 EndZ=0
    g1: LineSegment StartX=-13.2 StartY=-2 StartZ=0 EndX=-13.2 EndY=4.3 EndZ=0
    g2: LineSegment StartX=-13.2 StartY=4.3 StartZ=0 EndX=-21 EndY=4.3 EndZ=0
    g3: LineSegment StartX=-21 StartY=4.3 StartZ=0 EndX=-21 EndY=-2 EndZ=0
    g4: LineSegment StartX=-7.6 StartY=-2 StartZ=0 EndX=7.6 EndY=-2 EndZ=0
    g5: LineSegment StartX=7.6 StartY=-2 StartZ=0 EndX=7.6 EndY=8 EndZ=0
    g6: LineSegment StartX=7.6 StartY=8 StartZ=0 EndX=-7.6 EndY=8 EndZ=0
    g7: LineSegment StartX=-7.6 StartY=8 StartZ=0 EndX=-7.6 EndY=-2 EndZ=0
    g8: LineSegment StartX=18.75 StartY=-2 StartZ=0 EndX=24.05 EndY=-2 EndZ=0
    g9: LineSegment StartX=24.05 StartY=-2 StartZ=0 EndX=24.05 EndY=4.5 EndZ=0
    g10: LineSegment StartX=18.75 StartY=4.5 StartZ=0 EndX=18.75 EndY=-2 EndZ=0
    g11: GeomPoint X=21.4 Y=-2 Z=0
    g12: ArcOfCircle CenterX=21.4 CenterY=4.5 CenterZ=0 NormalX=0 NormalY=0 NormalZ=1 AngleXU=0 Radius=2.65 StartAngle=1e-16 EndAngle=3.14159
    g13: GeomPoint X=-17.1 Y=-2 Z=0
  constraints (38):
    c: Coincident(g0,g1)
    c: Coincident(g1,g2)
    c: Coincident(g2,g3)
    c: Coincident(g3,g0)
    c: Horizontal(g0)
    c: Horizontal(g2)
    c: Vertical(g1)
    c: Vertical(g3)
    c: Coincident(g4,g5)
    c: Coincident(g5,g6)
    c: Coincident(g6,g7)
    c: Coincident(g7,g4)
    c: Horizontal(g4)
    c: Vertical(g5)
    c: Vertical(g7)
    c: Coincident(g8,g9)
    c: Coincident(g10,g8)
    c: Horizontal(g8)
    c: Vertical(g9)
    c: Vertical(g10)
    c: Distance(g4) = 15.2
    c: Distance(g8) = 5.3
    c: Symmetric(g8,g8,g11)
    c: Coincident(g12,g10)
    c: Coincident(g12,g9)
    c: Horizontal(g10,g12)
    c: Horizontal(g12,g9)
    c: DistanceY(g-1,g2) = 4.3
    c: DistanceY(g-1,g5) = 8
    c: DistanceY(g-1,g12) = 4.5
    c: Symmetric(g6,g5,g-2)
    c: DistanceX(g-1,g11) = 21.4
    c: Symmetric(g0,g0,g13)
    c: DistanceX(g13,g-1) = 17.1
    c: Horizontal(g0,g4)
    c: Horizontal(g4,g8)
    c: DistanceX(g0,g0) = 7.8
    c: DistanceY(g4,g-1) = 2
FEATURE [PartDesign::Pocket] Pocket004  label="отверстия низ"
  BaseFeature = -> Pocket003
  Direction = (0,1,-2e-16)
  Length = 2
  Length2 = 5
  Profile = -> Sketch011
  ReferenceAxis = -> Sketch011 [N_Axis]
  Type = 0
FEATURE [PartDesign::Fillet] Fillet  label="сглаж внутр"
  Base = -> Pocket004 [Edge83,Edge74,Edge87]
  BaseFeature = -> Pocket004
  Radius = 6
  SupportTransform = false
  UseAllEdges = false
FEATURE [PartDesign::Fillet] Fillet003  label="сглаж внутр лев"
  Base = -> Fillet [Edge61]
  BaseFeature = -> Fillet
  Radius = 2
  SupportTransform = false
  UseAllEdges = false
FEATURE [PartDesign::Fillet] Fillet004  label="сглаж верх"
  Base = -> Fillet003 [Edge109,Edge127,Edge108]
  BaseFeature = -> Fillet003
  Radius = 8
  SupportTransform = false
  UseAllEdges = false
FEATURE [PartDesign::Fillet] Fillet005  label="сглаж верх лев"
  Base = -> Fillet004 [Edge6,Edge8,Edge9]
  BaseFeature = -> Fillet004
  Radius = 3
  SupportTransform = false
  UseAllEdges = false
FEATURE [PartDesign::Fillet] Fillet006  label="сглаж бок"
  Base = -> Fillet005 [Edge13,Edge32,Edge6,Edge3]
  BaseFeature = -> Fillet005
  Radius = 5.5
  SupportTransform = false
  UseAllEdges = false
FEATURE [PartDesign::Body] Body  label="top"
  Group = -> [Sketch,Pad,Sketch001,Pocket,Sketch002,Pad001,Sketch008,Pocket001,Sketch009,Pocket002,Sketch010,Pocket003,Sketch011,Pocket004,Fillet,Fillet003,Fillet004,Fillet005,Fillet006]
  Origin = -> Origin058
  Tip = -> Fillet006
FEATURE [Sketcher::SketchObject] Sketch012
  AttachmentOffset = pos=(0,0,-2) rot=(0,0,1;0rad)
  FullyConstrained = true
  MapMode = 5
  Placement = pos=(0,0,-2) rot=(0,0,1;0rad)
  Support = -> [XY_Plane060]
  sketch-geometry (4):
    g0: LineSegment StartX=-50 StartY=25 StartZ=0 EndX=50 EndY=25 EndZ=0
    g1: LineSegment StartX=50 StartY=25 StartZ=0 EndX=50 EndY=-25 EndZ=0
    g2: LineSegment StartX=50 StartY=-25 StartZ=0 EndX=-50 EndY=-25 EndZ=0
    g3: LineSegment StartX=-50 StartY=-25 StartZ=0 EndX=-50 EndY=25 EndZ=0
  constraints (11):
    c: Coincident(g0,g1)
    c: Coincident(g1,g2)
    c: Coincident(g2,g3)
    c: Coincident(g3,g0)
    c: Horizontal(g0)
    c: Horizontal(g2)
    c: Vertical(g1)
    c: Vertical(g3)
    c: DistanceY(g3,g3) = 50
    c: DistanceX(g0,g0) = 100
    c: Symmetric(g0,g1,g-1)
FEATURE [PartDesign::Pad] Pad006  label="основа"
  Direction = (0,0,-1)
  Length = 2
  Length2 = 10
  Profile = -> Sketch012
  ReferenceAxis = -> Sketch012 [N_Axis]
  Type = 0
  UseCustomVector = true
FEATURE [Sketcher::SketchObject] Sketch013
  FullyConstrained = true
  MapMode = 5
  Placement = pos=(0,0,-2) rot=(0,0,1;0rad)
  Support = -> [Pad006]
  sketch-geometry (20):
    g0: LineSegment StartX=-47.8 StartY=22.8 StartZ=0 EndX=47.8 EndY=22.8 EndZ=0
    g1: LineSegment StartX=47.8 StartY=22.8 StartZ=0 EndX=47.8 EndY=-22.8 EndZ=0
    g2: LineSegment StartX=47.8 StartY=-22.8 StartZ=0 EndX=-47.8 EndY=-22.8 EndZ=0
    g3: LineSegment StartX=-47.8 StartY=-22.8 StartZ=0 EndX=-47.8 EndY=22.8 EndZ=0
    g4: ArcOfCircle CenterX=-44 CenterY=19 CenterZ=0 NormalX=0 NormalY=0 NormalZ=1 AngleXU=0 Radius=4 StartAngle=4.71239 EndAngle=6.28319
    g5: ArcOfCircle CenterX=44 CenterY=19 CenterZ=0 NormalX=0 NormalY=0 NormalZ=1 AngleXU=0 Radius=4 StartAngle=3.14159 EndAngle=4.71239
    g6: ArcOfCircle CenterX=-44 CenterY=-19 CenterZ=0 NormalX=0 NormalY=0 NormalZ=1 AngleXU=0 Radius=4 StartAngle=2.08076e-08 EndAngle=1.5708
    g7: ArcOfCircle CenterX=44 CenterY=-19 CenterZ=0 NormalX=0 NormalY=0 NormalZ=1 AngleXU=0 Radius=4 StartAngle=1.5708 EndAngle=3.14159
    g8: LineSegment StartX=-44 StartY=-15 StartZ=0 EndX=-46 EndY=-15 EndZ=0
    g9: LineSegment StartX=-40 StartY=-19 StartZ=0 EndX=-40 EndY=-21 EndZ=0
    g10: LineSegment StartX=-44 StartY=15 StartZ=0 EndX=-46 EndY=15 EndZ=0
    g11: LineSegment StartX=-40 StartY=19 StartZ=0 EndX=-40 EndY=21 EndZ=0
    g12: LineSegment StartX=40 StartY=19 StartZ=0 EndX=40 EndY=21 EndZ=0
    g13: LineSegment StartX=44 StartY=15 StartZ=0 EndX=46 EndY=15 EndZ=0
    g14: LineSegment StartX=44 StartY=-15 StartZ=0 EndX=46 EndY=-15 EndZ=0
    g15: LineSegment StartX=40 StartY=-19 StartZ=0 EndX=40 EndY=-21 EndZ=0
    g16: LineSegment StartX=-40 StartY=-21 StartZ=0 EndX=40 EndY=-21 EndZ=0
    g17: LineSegment StartX=-46 StartY=-15 StartZ=0 EndX=-46 EndY=15 EndZ=0
    g18: LineSegment StartX=-40 StartY=21 StartZ=0 EndX=40 EndY=21 EndZ=0
    g19: LineSegment StartX=46 StartY=15 StartZ=0 EndX=46 EndY=-15 EndZ=0
  constraints (63):
    c: Coincident(g0,g1)
    c: Coincident(g1,g2)
    c: Coincident(g2,g3)
    c: Coincident(g3,g0)
    c: Horizontal(g0)
    c: Horizontal(g2)
    c: Vertical(g1)
    c: Vertical(g3)
    c: DistanceX(g0,g0) = 95.6
    c: DistanceY(g3,g3) = 45.6
    c: Symmetric(g0,g1,g-1)
    c: DistanceY(g4,g0) = 3.8
    c: DistanceY(g2,g6) = 3.8
    c: DistanceX(g7,g1) = 3.8
    c: DistanceX(g0,g4) = 3.8
    c: Radius(g4) = 4
    c: Radius(g5) = 4
    c: Radius(g7) = 4
    c: Radius(g6) = 4
    c: Coincident(g8,g6)
    c: Horizontal(g8)
    c: Coincident(g9,g6)
    c: Vertical(g9)
    c: Coincident(g10,g4)
    c: Horizontal(g10)
    c: Coincident(g11,g4)
    c: Vertical(g11)
    c: Coincident(g12,g5)
    c: Vertical(g12)
    c: Coincident(g13,g5)
    c: Horizontal(g13)
    c: Coincident(g14,g7)
    c: Horizontal(g14)
    c: Coincident(g15,g7)
    c: Vertical(g15)
    c: DistanceX(g14,g14) = 2
    c: DistanceX(g8,g8) = 2
    c: DistanceX(g10,g10) = 2
    c: DistanceX(g13,g13) = 2
    c: DistanceY(g12,g12) = 2
    c: DistanceY(g11,g11) = 2
    c: DistanceY(g9,g9) = 2
    c: DistanceY(g15,g15) = 2
    c: Coincident(g16,g9)
    c: Horizontal(g16)
    c: Coincident(g17,g8)
    c: Vertical(g17)
    c: Coincident(g18,g11)
    c: Horizontal(g18)
    c: Coincident(g19,g13)
    c: Vertical(g19)
    c: Coincident(g17,g10)
    c: Coincident(g18,g12)
    c: Coincident(g19,g14)
    c: Coincident(g16,g15)
    c: DistanceX(g0,g10) = 1.8
    c: DistanceX(g14,g1) = 1.8
    c: DistanceX(g0,g11) = 7.8
    c: Vertical(g6,g4)
    c: Vertical(g6,g4)
    c: Horizontal(g6,g7)
    c: Vertical(g5,g7)
    c: Horizontal(g5,g4)
FEATURE [PartDesign::Pad] Pad007  label="внутр грань"
  BaseFeature = -> Pad006
  Direction = (0,0,1)
  Length = 2
  Length2 = 10
  Profile = -> Sketch013
  ReferenceAxis = -> Sketch013 [N_Axis]
  Type = 0
FEATURE [Sketcher::SketchObject] Sketch014
  FullyConstrained = true
  MapMode = 5
  Placement = pos=(0,0,-2) rot=(0,0,1;0rad)
  Support = -> [Pad007]
  sketch-geometry (14):
    g0: LineSegment StartX=-20.8 StartY=-22.8 StartZ=0 EndX=-13.4 EndY=-22.8 EndZ=0
    g1: LineSegment StartX=-13.4 StartY=-22.8 StartZ=0 EndX=-13.4 EndY=-25 EndZ=0
    g2: LineSegment StartX=-13.4 StartY=-25 StartZ=0 EndX=-20.8 EndY=-25 EndZ=0
    g3: LineSegment StartX=-20.8 StartY=-25 StartZ=0 EndX=-20.8 EndY=-22.8 EndZ=0
    g4: LineSegment StartX=-7.4 StartY=-22.8 StartZ=0 EndX=7.4 EndY=-22.8 EndZ=0
    g5: LineSegment StartX=7.4 StartY=-22.8 StartZ=0 EndX=7.4 EndY=-25 EndZ=0
    g6: LineSegment StartX=7.4 StartY=-25 StartZ=0 EndX=-7.4 EndY=-25 EndZ=0
    g7: LineSegment StartX=-7.4 StartY=-25 StartZ=0 EndX=-7.4 EndY=-22.8 EndZ=0
    g8: LineSegment StartX=18.95 StartY=-22.8 StartZ=0 EndX=23.85 EndY=-22.8 EndZ=0
    g9: LineSegment StartX=23.85 StartY=-22.8 StartZ=0 EndX=23.85 EndY=-25 EndZ=0
    g10: LineSegment StartX=23.85 StartY=-25 StartZ=0 EndX=18.95 EndY=-25 EndZ=0
    g11: LineSegment StartX=18.95 StartY=-25 StartZ=0 EndX=18.95 EndY=-22.8 EndZ=0
    g12: GeomPoint X=-17.1 Y=-25 Z=0
    g13: GeomPoint X=21.4 Y=-25 Z=0
  constraints (37):
    c: Coincident(g0,g1)
    c: Coincident(g1,g2)
    c: Coincident(g2,g3)
    c: Coincident(g3,g0)
    c: Horizontal(g0)
    c: Horizontal(g2)
    c: Vertical(g1)
    c: Vertical(g3)
    c: Coincident(g4,g5)
    c: Coincident(g5,g6)
    c: Coincident(g6,g7)
    c: Coincident(g7,g4)
    c: Horizontal(g4)
    c: Vertical(g5)
    c: Vertical(g7)
    c: Coincident(g8,g9)
    c: Coincident(g9,g10)
    c: Coincident(g10,g11)
    c: Coincident(g11,g8)
    c: Horizontal(g8)
    c: Horizontal(g10)
    c: Vertical(g9)
    c: Vertical(g11)
    c: DistanceY(g3,g3) = 2.2
    c: Horizontal(g1,g6)
    c: Horizontal(g5,g10)
    c: Horizontal(g0,g4)
    c: Horizontal(g4,g8)
    c: DistanceX(g6,g6) = 14.8
    c: DistanceX(g10,g10) = 4.9
    c: DistanceX(g2,g2) = 7.4
    c: Symmetric(g6,g5,g-2)
    c: DistanceX(g12,g-1) = 17.1
    c: DistanceX(g-1,g13) = 21.4
    c: Symmetric(g2,g1,g12)
    c: Symmetric(g10,g9,g13)
    c: DistanceY(g6,g-1) = 25
FEATURE [PartDesign::Pad] Pad008  label="заглушки нижних отверстий"
  BaseFeature = -> Pad007
  Direction = (0,0,1)
  Length = 3.6
  Length2 = 10
  Profile = -> Sketch014
  ReferenceAxis = -> Sketch014 [N_Axis]
  Type = 0
FEATURE [Sketcher::SketchObject] Sketch015
  ExternalGeometry = -> [Pad008]
  FullyConstrained = true
  MapMode = 5
  Placement = pos=(0,0,-4) rot=(1,0,0;3.14159rad)
  Support = -> [Pad008]
  sketch-geometry (4):
    g0: Circle CenterX=-44 CenterY=19 CenterZ=0 NormalX=0 NormalY=0 NormalZ=1 AngleXU=0 Radius=1.6
    g1: Circle CenterX=44 CenterY=19 CenterZ=0 NormalX=0 NormalY=0 NormalZ=1 AngleXU=0 Radius=1.6
    g2: Circle CenterX=-44 CenterY=-19 CenterZ=0 NormalX=0 NormalY=0 NormalZ=1 AngleXU=0 Radius=1.6
    g3: Circle CenterX=44 CenterY=-19 CenterZ=0 NormalX=0 NormalY=0 NormalZ=1 AngleXU=0 Radius=1.6
  constraints (12):
    c: Radius(g0) = 1.6
    c: Radius(g2) = 1.6
    c: Radius(g3) = 1.6
    c: Radius(g1) = 1.6
    c: DistanceX(g-3,g0) = 6
    c: DistanceX(g-4,g2) = 6
    c: DistanceX(g3,g-5) = 6
    c: DistanceX(g1,g-6) = 6
    c: DistanceY(g0,g-3) = 6
    c: DistanceY(g-4,g2) = 6
    c: DistanceY(g-5,g3) = 6
    c: DistanceY(g1,g-6) = 6
FEATURE [PartDesign::Pocket] Pocket005  label="отверстия"
  BaseFeature = -> Pad008
  Direction = (0,0,1)
  Length = 5
  Length2 = 5
  Profile = -> Sketch015
  ReferenceAxis = -> Sketch015 [N_Axis]
  Type = 1
FEATURE [Sketcher::SketchObject] Sketch016
  ExternalGeometry = -> [Pocket005]
  FullyConstrained = true
  MapMode = 5
  Placement = pos=(0,0,-4) rot=(1,0,0;3.14159rad)
  Support = -> [Pocket005]
  sketch-geometry (4):
    g0: Circle CenterX=-44 CenterY=19 CenterZ=0 NormalX=0 NormalY=0 NormalZ=1 AngleXU=0 Radius=3
    g1: Circle CenterX=44 CenterY=19 CenterZ=0 NormalX=0 NormalY=0 NormalZ=1 AngleXU=0 Radius=3
    g2: Circle CenterX=44 CenterY=-19 CenterZ=0 NormalX=0 NormalY=0 NormalZ=1 AngleXU=0 Radius=3
    g3: Circle CenterX=-44 CenterY=-19 CenterZ=0 NormalX=0 NormalY=0 NormalZ=1 AngleXU=0 Radius=3
  constraints (12):
    c: Radius(g0) = 3
    c: Radius(g1) = 3
    c: Radius(g3) = 3
    c: Radius(g2) = 3
    c: DistanceY(g0,g-3) = 6
    c: DistanceY(g-6,g3) = 6
    c: DistanceY(g-5,g2) = 6
    c: DistanceY(g1,g-4) = 6
    c: DistanceX(g-3,g0) = 6
    c: DistanceX(g1,g-4) = 6
    c: DistanceX(g-6,g3) = 6
    c: DistanceX(g2,g-5) = 6
FEATURE [PartDesign::Pocket] Pocket006  label="заглубления под винты"
  BaseFeature = -> Pocket005
  Direction = (0,0,1)
  Length = 1.8
  Length2 = 5
  Profile = -> Sketch016
  ReferenceAxis = -> Sketch016 [N_Axis]
  Type = 0
FEATURE [PartDesign::Fillet] Fillet007  label="сглаж"
  Base = -> Pocket006 [Edge8,Edge2]
  BaseFeature = -> Pocket006
  Radius = 5.5
  SupportTransform = false
  UseAllEdges = false
FEATURE [PartDesign::Fillet] Fillet008  label="сглаж лев"
  Base = -> Fillet007 [Edge3,Edge20]
  BaseFeature = -> Fillet007
  Radius = 3
  SupportTransform = false
  UseAllEdges = false
FEATURE [PartDesign::Body] Body002  label="bottom"
  Group = -> [Sketch012,Pad006,Sketch013,Pad007,Sketch014,Pad008,Sketch015,Pocket005,Sketch016,Pocket006,Fillet007,Fillet008]
  Origin = -> Origin060
  Tip = -> Fillet008
